# Revit family: AB-AS1565xWS840MPO0400
name_source: partatom
category: Leuchten
units: mm (PartAtom-declared; Revit-internal decimal feet)

## family parameters
Basisbauteil = Fläche
Beim Laden mit Abzugskörper schneiden = Nein
Bemaßung runder Anschluss = Durchmesser verwenden
Gemeinsam genutzt = Nein
Lichtquelle = Ja
OmniClass-Nummer = 23.80.70.11
OmniClass-Titel = Luminaries for Internal Lighting
Raumberechnungspunkt = Nein
Teiletyp = Normal

## types (2) — shared parameters
Baugruppenkennzeichen = D5020200
Datei für fotometrisches Netz = AB-AS_MPO.IES
Emissionsform beim Rendern sichtbar = Nein
Farbfilter = 16777215
Farbtemperaturverschiebung bei Dämpfen der Lampe = <Keine Auswahl>
Hersteller = RIDI Leuchten GmbH
Lampe = LED
Neigungswinkel = 90.00°
Scheinlast = 32 VA
URL = www.ridi.de
Von Breite des Rechtecks ausssenden = 1502 mm  [stored 4.92782 ft]
Von Länge des Rechtecks aussenden = 132 mm  [stored 0.433071 ft]
brand = RIDI
conformity mark = CE
electrical safety class = 1
height = 55 mm  [stored 0.180446 ft]
ingress protection (IP) code = IP40
length = 1565 mm  [stored 5.13451 ft]
nominal frequency = 50-60Hz
nominal voltage = 230
rated input power = 32
voltage type (AC, DC, UC) = AC
weight = 5,2kg
width = 200 mm  [stored 0.656168 ft]
zero-valued in all types: Vorgabe-Ansicht

## per-type parameters (varying)
| type | Modell | product name |
| AB-AS1565FLWS840MPO0400 | 0627923 | AB-AS1265FLWS840MPO0350
EL-AQ0622NDWS840M9P0400
AB-AS1565FLWS840MPO0400 |
| AB-AS1565DAWS840MPO0400 | 0637923 | AB-AS1565DAWS840MPO0400 |

note: [stored X ft] marks values corroborated as IEEE doubles in the binary element streams (Revit-internal decimal feet)
